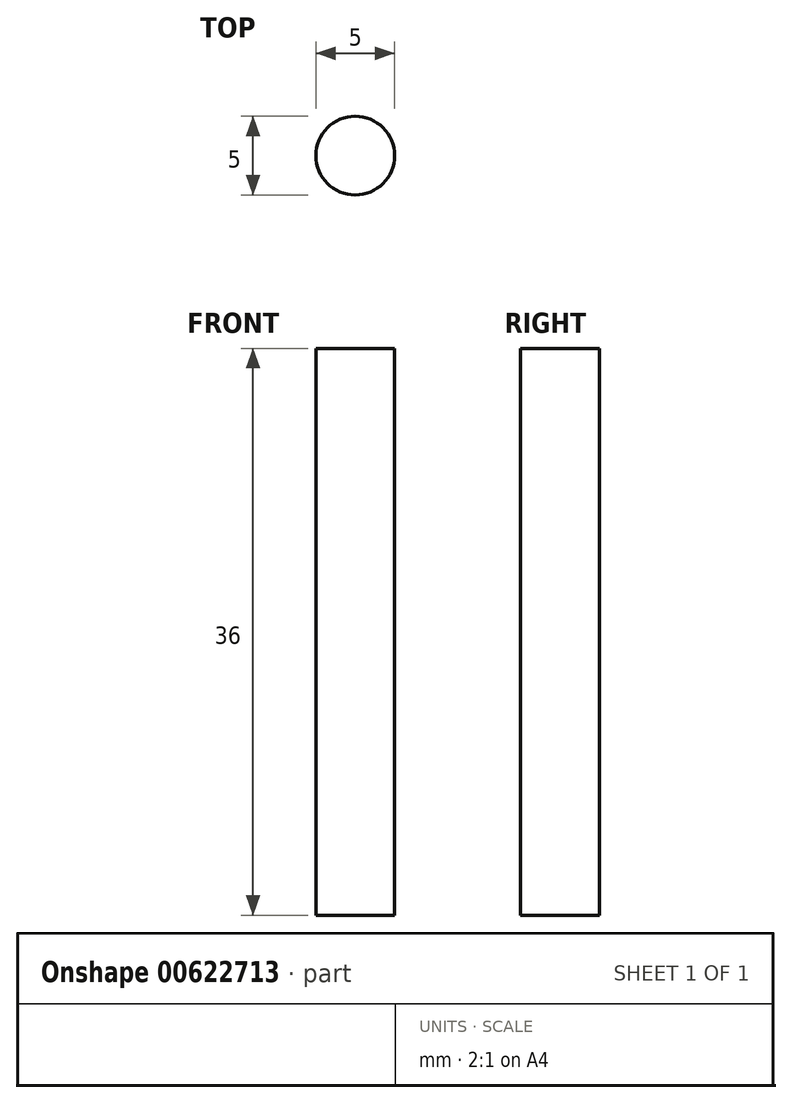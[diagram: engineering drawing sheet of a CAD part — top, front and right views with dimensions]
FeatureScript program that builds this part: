
annotation { "Feature Type Name" : "Feature", "Feature Type Description" : "" }
export const myFeature = defineFeature(function(context is Context, id is Id, definition is map)
    precondition{}
    {
        {
            var Q0;
            Q0=qCreatedBy(makeId("Top.planeOp"),FACE);
            var sketch = newSketch(context, id + "F0", { "sketchPlane" : qUnion([Q0])});
            skCircle(sketch, "E0", {"center": v(0, 0) * mm, "radius": 2.5 * mm});
            skSolve(sketch);
        }
        {
            var Q0;
            Q0=makeQuery(id+"F0.imprint","IMPRINT",FACE,{"disambiguationData":[TD([[makeQuery(id+"F0.imprint","IMPRINT",EDGE,{"derivedFrom":sQuery(id+"F0.wireOp",EDGE,"E0")}),1.0]])]});
            extrude(context, id + "F1", {"entities" : qUnion([Q0]), "depth" : 36 * mm, "offsetDistance" : 25 * mm});
        }
    });
